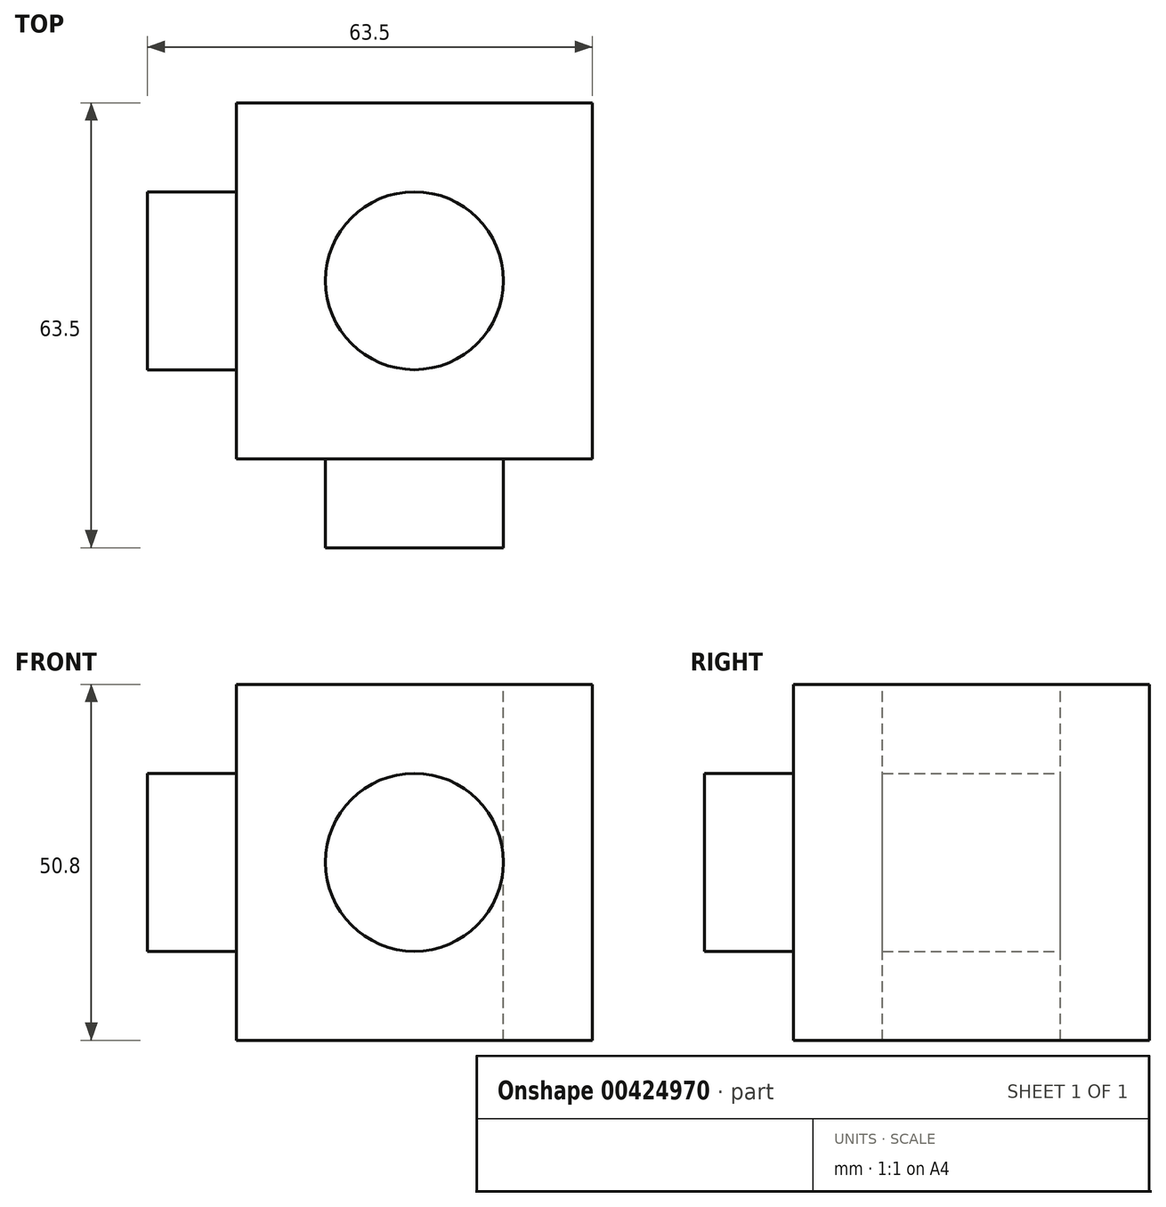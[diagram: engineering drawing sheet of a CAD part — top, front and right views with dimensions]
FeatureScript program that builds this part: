
annotation { "Feature Type Name" : "Feature", "Feature Type Description" : "" }
export const myFeature = defineFeature(function(context is Context, id is Id, definition is map)
    precondition{}
    {
        {
            var Q0;
            Q0=qCreatedBy(makeId("Front.planeOp"),FACE);
            var sketch = newSketch(context, id + "F0", { "sketchPlane" : qUnion([Q0])});
            skLineSegment(sketch, "E0.bottom", {"start": v(0, 0) * mm, "end": v(-50.8, 0) * mm});
            skLineSegment(sketch, "E0.top", {"start": v(0, 50.8) * mm, "end": v(-50.8, 50.8) * mm});
            skLineSegment(sketch, "E0.left", {"start": v(0, 0) * mm, "end": v(0, 50.8) * mm});
            skLineSegment(sketch, "E0.right", {"start": v(-50.8, 0) * mm, "end": v(-50.8, 50.8) * mm});
            skSolve(sketch);
        }
        {
            var Q0;
            Q0 = qSketchRegion(id + "F0", true);
            extrude(context, id + "F1", {"entities" : qUnion([Q0]), "depth" : 50.8 * mm});
        }
        {
            var Q0;
            Q0=makeQuery(id+"F1.opExtrude","CAP_FACE",FACE,{"disambiguationData":[OSD([sQuery(id+"F0.wireOp",EDGE,"E0.bottom"),sQuery(id+"F0.wireOp",EDGE,"E0.top"),sQuery(id+"F0.wireOp",EDGE,"E0.left"),sQuery(id+"F0.wireOp",EDGE,"E0.right")])],"isStart":false});
            var sketch = newSketch(context, id + "F2", { "sketchPlane" : qUnion([Q0])});
            skCircle(sketch, "E1", {"center": v(-25.4, 25.4) * mm, "radius": 12.7 * mm});
            skSolve(sketch);
        }
        {
            var Q0;
            Q0 = qSketchRegion(id + "F2", true);
            extrude(context, id + "F3", {"entities" : qUnion([Q0]), "operationType" : NewBodyOperationType.ADD, "depth" : 12.7 * mm});
        }
        {
            var Q0;
            Q0=makeQuery(id+"F1.opExtrude","SWEPT_FACE",FACE,{"disambiguationData":[OSD([sQuery(id+"F0.wireOp",EDGE,"E0.top")])]});
            var sketch = newSketch(context, id + "F4", { "sketchPlane" : qUnion([Q0])});
            skCircle(sketch, "E2", {"center": v(-25.4, -25.4) * mm, "radius": 12.7 * mm});
            skSolve(sketch);
        }
        {
            var Q0;
            Q0 = qSketchRegion(id + "F4", true);
            extrude(context, id + "F5", {"entities" : qUnion([Q0]), "operationType" : NewBodyOperationType.REMOVE, "oppositeDirection" : true, "depth" : 50.8 * mm});
        }
        {
            var Q0;
            Q0=makeQuery(id+"F1.opExtrude","SWEPT_FACE",FACE,{"disambiguationData":[OSD([sQuery(id+"F0.wireOp",EDGE,"E0.right")])]});
            var sketch = newSketch(context, id + "F6", { "sketchPlane" : qUnion([Q0])});
            skLineSegment(sketch, "E3.bottom", {"start": v(38.1, 12.7) * mm, "end": v(12.7, 12.7) * mm});
            skLineSegment(sketch, "E3.top", {"start": v(38.1, 38.1) * mm, "end": v(12.7, 38.1) * mm});
            skLineSegment(sketch, "E3.left", {"start": v(38.1, 12.7) * mm, "end": v(38.1, 38.1) * mm});
            skLineSegment(sketch, "E3.right", {"start": v(12.7, 12.7) * mm, "end": v(12.7, 38.1) * mm});
            skSolve(sketch);
        }
        {
            var Q0;
            Q0 = qSketchRegion(id + "F6", true);
            extrude(context, id + "F7", {"entities" : qUnion([Q0]), "operationType" : NewBodyOperationType.ADD, "depth" : 12.7 * mm});
        }
    });
